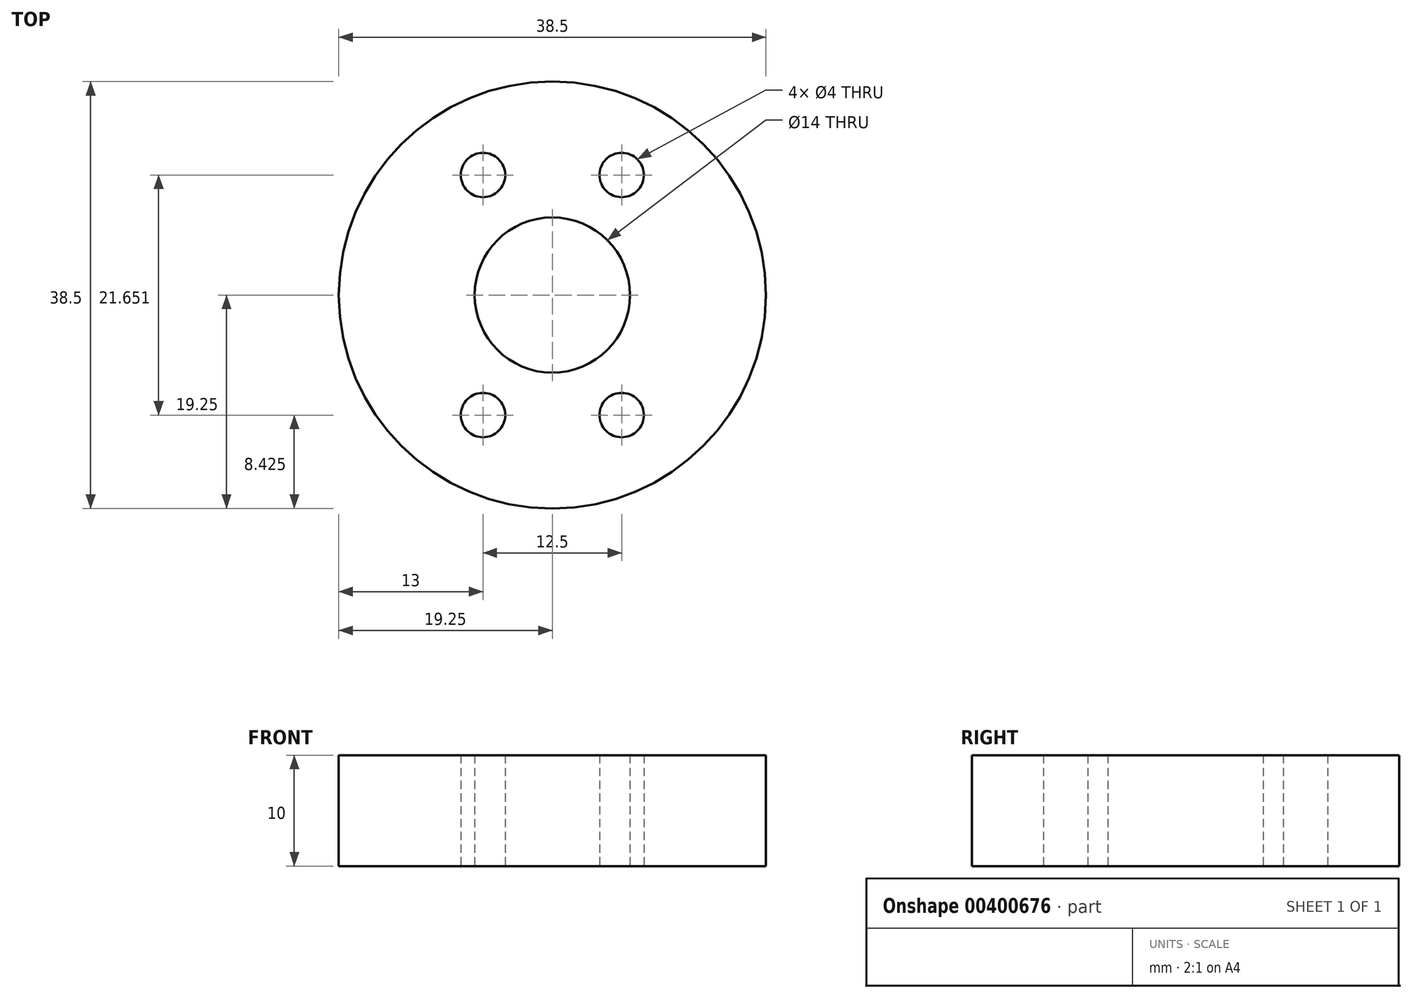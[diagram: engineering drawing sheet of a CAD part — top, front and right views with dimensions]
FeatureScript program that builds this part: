
annotation { "Feature Type Name" : "Feature", "Feature Type Description" : "" }
export const myFeature = defineFeature(function(context is Context, id is Id, definition is map)
    precondition{}
    {
        {
            var Q0;
            Q0=qCreatedBy(makeId("Top.planeOp"),FACE);
            var sketch = newSketch(context, id + "F0", { "sketchPlane" : qUnion([Q0])});
            skCircle(sketch, "E0", {"center": v(0, 0) * mm, "radius": 19.25 * mm});
            skPoint(sketch, "E1", {"position": v(-19.25, 0) * mm});
            skPoint(sketch, "E2", {"position": v(19.25, 0) * mm});
            skPoint(sketch, "E3", {"position": v(0, -19.25) * mm});
            skPoint(sketch, "E4", {"position": v(0, 19.25) * mm});
            skCircle(sketch, "E5", {"center": v(0, 0) * mm, "radius": 12.5 * mm});
            skPoint(sketch, "E6", {"position": v(-6.25, 10.83) * mm});
            skPoint(sketch, "E7", {"position": v(6.25, 10.83) * mm});
            skPoint(sketch, "E8", {"position": v(6.25, -10.83) * mm});
            skPoint(sketch, "E9", {"position": v(-6.25, -10.83) * mm});
            skPoint(sketch, "E10.center.orphan", {"position": v(12.5, 0) * mm});
            skPoint(sketch, "E11.center.orphan", {"position": v(-12.5, 0) * mm});
            skCircle(sketch, "E12", {"center": v(-6.25, 10.83) * mm, "radius": 2 * mm});
            skCircle(sketch, "E13", {"center": v(0, 0) * mm, "radius": 7 * mm});
            skCircle(sketch, "E14", {"center": v(6.25, 10.83) * mm, "radius": 2 * mm});
            skCircle(sketch, "E15", {"center": v(6.25, -10.83) * mm, "radius": 2 * mm});
            skCircle(sketch, "E16", {"center": v(-6.25, -10.83) * mm, "radius": 2 * mm});
            skSolve(sketch);
        }
        {
            var Q0;
            Q0 = qSketchRegion(id + "F0", true);
            var Q1;
            Q1=makeQuery(id+"F0.imprint","IMPRINT",FACE,{"disambiguationData":[TD([[makeQuery(id+"F0.imprint","IMPRINT",EDGE,{"derivedFrom":sQuery(id+"F0.wireOp",EDGE,"E13")}),-1.0]])]});
            extrude(context, id + "F1", {"entities" : qUnion([Q0, Q1]), "depth" : 10 * mm});
        }
    });
